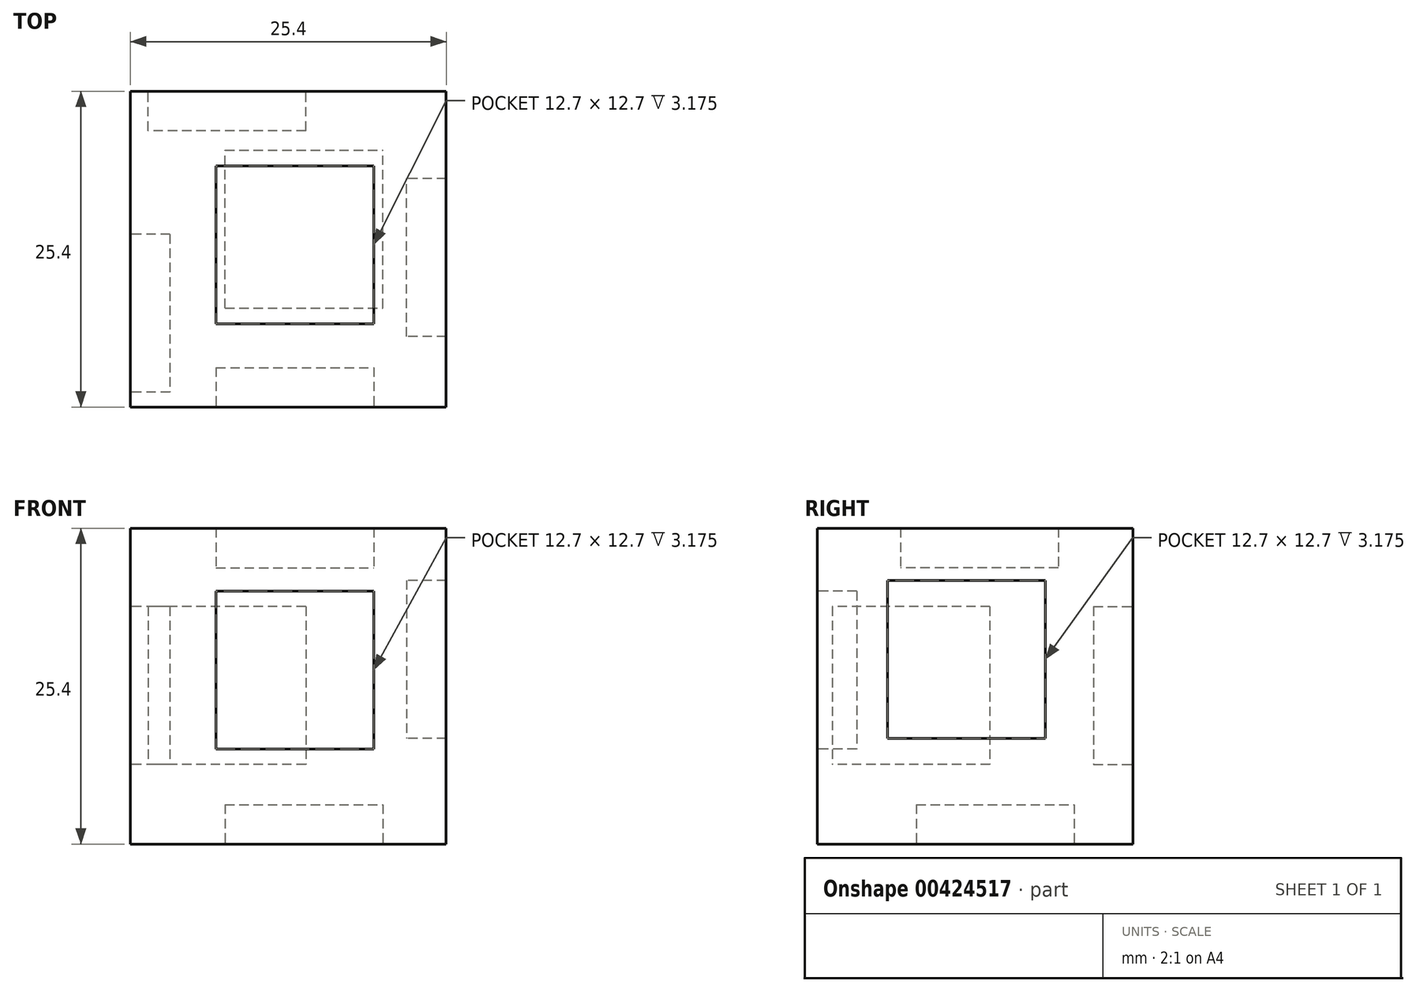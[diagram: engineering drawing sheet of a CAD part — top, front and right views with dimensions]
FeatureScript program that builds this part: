
annotation { "Feature Type Name" : "Feature", "Feature Type Description" : "" }
export const myFeature = defineFeature(function(context is Context, id is Id, definition is map)
    precondition{}
    {
        {
            var Q0;
            Q0=qCreatedBy(makeId("Front.planeOp"),FACE);
            var sketch = newSketch(context, id + "F0", { "sketchPlane" : qUnion([Q0])});
            skLineSegment(sketch, "E0.bottom", {"start": v(-14.1, -6.4) * mm, "end": v(11.3, -6.4) * mm});
            skLineSegment(sketch, "E0.top", {"start": v(-14.1, 19) * mm, "end": v(11.3, 19) * mm});
            skLineSegment(sketch, "E0.left", {"start": v(-14.1, -6.4) * mm, "end": v(-14.1, 19) * mm});
            skLineSegment(sketch, "E0.right", {"start": v(11.3, -6.4) * mm, "end": v(11.3, 19) * mm});
            skSolve(sketch);
        }
        {
            var Q0;
            Q0=makeQuery(id+"F0.imprint","IMPRINT",FACE,{"disambiguationData":[TD([[makeQuery(id+"F0.imprint","IMPRINT",EDGE,{"derivedFrom":sQuery(id+"F0.wireOp",EDGE,"E0.bottom")}),1.0]])]});
            extrude(context, id + "F1", {"entities" : qUnion([Q0]), "depth" : 25.4 * mm});
        }
        {
            var Q0;
            Q0=makeQuery(id+"F1.opExtrude","CAP_FACE",FACE,{"disambiguationData":[OSD([sQuery(id+"F0.wireOp",EDGE,"E0.bottom"),sQuery(id+"F0.wireOp",EDGE,"E0.top"),sQuery(id+"F0.wireOp",EDGE,"E0.left"),sQuery(id+"F0.wireOp",EDGE,"E0.right")])],"isStart":false});
            var sketch = newSketch(context, id + "F2", { "sketchPlane" : qUnion([Q0])});
            skLineSegment(sketch, "E1.bottom", {"start": v(-7.21, 13.93) * mm, "end": v(5.49, 13.93) * mm});
            skLineSegment(sketch, "E1.top", {"start": v(-7.21, 1.23) * mm, "end": v(5.49, 1.23) * mm});
            skLineSegment(sketch, "E1.left", {"start": v(-7.21, 13.93) * mm, "end": v(-7.21, 1.23) * mm});
            skLineSegment(sketch, "E1.right", {"start": v(5.49, 13.93) * mm, "end": v(5.49, 1.23) * mm});
            skSolve(sketch);
        }
        {
            var Q0;
            Q0=makeQuery(id+"F2.imprint","IMPRINT",FACE,{"disambiguationData":[TD([[makeQuery(id+"F2.imprint","IMPRINT",EDGE,{"derivedFrom":sQuery(id+"F2.wireOp",EDGE,"E1.bottom")}),-1.0]])]});
            extrude(context, id + "F3", {"entities" : qUnion([Q0]), "operationType" : NewBodyOperationType.REMOVE, "oppositeDirection" : true, "depth" : 3.17 * mm});
        }
        {
            var Q0;
            Q0=makeQuery(id+"F1.opExtrude","SWEPT_FACE",FACE,{"disambiguationData":[OSD([sQuery(id+"F0.wireOp",EDGE,"E0.bottom")])]});
            var sketch = newSketch(context, id + "F4", { "sketchPlane" : qUnion([Q0])});
            skLineSegment(sketch, "E2.bottom", {"start": v(-6.5, 17.43) * mm, "end": v(6.2, 17.43) * mm});
            skLineSegment(sketch, "E2.top", {"start": v(-6.5, 4.73) * mm, "end": v(6.2, 4.73) * mm});
            skLineSegment(sketch, "E2.left", {"start": v(-6.5, 17.43) * mm, "end": v(-6.5, 4.73) * mm});
            skLineSegment(sketch, "E2.right", {"start": v(6.2, 17.43) * mm, "end": v(6.2, 4.73) * mm});
            skSolve(sketch);
        }
        {
            var Q0;
            Q0=makeQuery(id+"F4.imprint","IMPRINT",FACE,{"disambiguationData":[TD([[makeQuery(id+"F4.imprint","IMPRINT",EDGE,{"derivedFrom":sQuery(id+"F4.wireOp",EDGE,"E2.bottom")}),-1.0]])]});
            extrude(context, id + "F5", {"entities" : qUnion([Q0]), "operationType" : NewBodyOperationType.REMOVE, "oppositeDirection" : true, "depth" : 3.17 * mm});
        }
        {
            var Q0;
            Q0=makeQuery(id+"F1.opExtrude","SWEPT_FACE",FACE,{"disambiguationData":[OSD([sQuery(id+"F0.wireOp",EDGE,"E0.right")])]});
            var sketch = newSketch(context, id + "F6", { "sketchPlane" : qUnion([Q0])});
            skLineSegment(sketch, "E3.bottom", {"start": v(-19.73, 14.8) * mm, "end": v(-7.03, 14.8) * mm});
            skLineSegment(sketch, "E3.top", {"start": v(-19.73, 2.1) * mm, "end": v(-7.03, 2.1) * mm});
            skLineSegment(sketch, "E3.left", {"start": v(-19.73, 14.8) * mm, "end": v(-19.73, 2.1) * mm});
            skLineSegment(sketch, "E3.right", {"start": v(-7.03, 14.8) * mm, "end": v(-7.03, 2.1) * mm});
            skSolve(sketch);
        }
        {
            var Q0;
            Q0=makeQuery(id+"F6.imprint","IMPRINT",FACE,{"disambiguationData":[TD([[makeQuery(id+"F6.imprint","IMPRINT",EDGE,{"derivedFrom":sQuery(id+"F6.wireOp",EDGE,"E3.bottom")}),-1.0]])]});
            extrude(context, id + "F7", {"entities" : qUnion([Q0]), "operationType" : NewBodyOperationType.REMOVE, "oppositeDirection" : true, "depth" : 3.17 * mm});
        }
        {
            var Q0;
            Q0=makeQuery(id+"F1.opExtrude","CAP_FACE",FACE,{"disambiguationData":[OSD([sQuery(id+"F0.wireOp",EDGE,"E0.bottom"),sQuery(id+"F0.wireOp",EDGE,"E0.top"),sQuery(id+"F0.wireOp",EDGE,"E0.left"),sQuery(id+"F0.wireOp",EDGE,"E0.right")])],"isStart":true});
            var sketch = newSketch(context, id + "F8", { "sketchPlane" : qUnion([Q0])});
            skLineSegment(sketch, "E4.bottom", {"start": v(0, 12.7) * mm, "end": v(12.7, 12.7) * mm});
            skLineSegment(sketch, "E4.top", {"start": v(0, 0) * mm, "end": v(12.7, 0) * mm});
            skLineSegment(sketch, "E4.left", {"start": v(0, 12.7) * mm, "end": v(0, 0) * mm});
            skLineSegment(sketch, "E4.right", {"start": v(12.7, 12.7) * mm, "end": v(12.7, 0) * mm});
            skSolve(sketch);
        }
        {
            var Q0;
            Q0=makeQuery(id+"F8.imprint","IMPRINT",FACE,{"disambiguationData":[TD([[makeQuery(id+"F8.imprint","IMPRINT",EDGE,{"derivedFrom":sQuery(id+"F8.wireOp",EDGE,"E4.bottom")}),-1.0]])]});
            extrude(context, id + "F9", {"entities" : qUnion([Q0]), "operationType" : NewBodyOperationType.REMOVE, "oppositeDirection" : true, "depth" : 3.17 * mm});
        }
        {
            var Q0;
            Q0=makeQuery(id+"F1.opExtrude","SWEPT_FACE",FACE,{"disambiguationData":[OSD([sQuery(id+"F0.wireOp",EDGE,"E0.left")])]});
            var sketch = newSketch(context, id + "F10", { "sketchPlane" : qUnion([Q0])});
            skLineSegment(sketch, "E5.bottom", {"start": v(11.5, 12.7) * mm, "end": v(24.2, 12.7) * mm});
            skLineSegment(sketch, "E5.top", {"start": v(11.5, 0) * mm, "end": v(24.2, 0) * mm});
            skLineSegment(sketch, "E5.left", {"start": v(11.5, 12.7) * mm, "end": v(11.5, 0) * mm});
            skLineSegment(sketch, "E5.right", {"start": v(24.2, 12.7) * mm, "end": v(24.2, 0) * mm});
            skSolve(sketch);
        }
        {
            var Q0;
            Q0=makeQuery(id+"F10.imprint","IMPRINT",FACE,{"disambiguationData":[TD([[makeQuery(id+"F10.imprint","IMPRINT",EDGE,{"derivedFrom":sQuery(id+"F10.wireOp",EDGE,"E5.bottom")}),-1.0]])]});
            extrude(context, id + "F11", {"entities" : qUnion([Q0]), "operationType" : NewBodyOperationType.REMOVE, "oppositeDirection" : true, "depth" : 3.17 * mm});
        }
        {
            var Q0;
            Q0=makeQuery(id+"F1.opExtrude","SWEPT_FACE",FACE,{"disambiguationData":[OSD([sQuery(id+"F0.wireOp",EDGE,"E0.top")])]});
            var sketch = newSketch(context, id + "F12", { "sketchPlane" : qUnion([Q0])});
            skLineSegment(sketch, "E6.bottom", {"start": v(-7.21, -6) * mm, "end": v(5.49, -6) * mm});
            skLineSegment(sketch, "E6.top", {"start": v(-7.21, -18.7) * mm, "end": v(5.49, -18.7) * mm});
            skLineSegment(sketch, "E6.left", {"start": v(-7.21, -6) * mm, "end": v(-7.21, -18.7) * mm});
            skLineSegment(sketch, "E6.right", {"start": v(5.49, -6) * mm, "end": v(5.49, -18.7) * mm});
            skSolve(sketch);
        }
        {
            var Q0;
            Q0=makeQuery(id+"F12.imprint","IMPRINT",FACE,{"disambiguationData":[TD([[makeQuery(id+"F12.imprint","IMPRINT",EDGE,{"derivedFrom":sQuery(id+"F12.wireOp",EDGE,"E6.bottom")}),-1.0]])]});
            extrude(context, id + "F13", {"entities" : qUnion([Q0]), "operationType" : NewBodyOperationType.REMOVE, "oppositeDirection" : true, "depth" : 3.17 * mm});
        }
        {
            var Q0;
            Q0=makeQuery(id+"F13.boolean.opBoolean","COPY",FACE,{"derivedFrom":makeQuery(id+"F13.opExtrude","CAP_FACE",FACE,{"disambiguationData":[OSD([sQuery(id+"F12.wireOp",EDGE,"E6.bottom"),sQuery(id+"F12.wireOp",EDGE,"E6.top"),sQuery(id+"F12.wireOp",EDGE,"E6.left"),sQuery(id+"F12.wireOp",EDGE,"E6.right")])],"isStart":false})});
            var sketch = newSketch(context, id + "F14", { "sketchPlane" : qUnion([Q0])});
            skLineSegment(sketch, "E7.bottom", {"start": v(-7.21, -6) * mm, "end": v(5.49, -6) * mm});
            skLineSegment(sketch, "E7.top", {"start": v(-7.21, -18.7) * mm, "end": v(5.49, -18.7) * mm});
            skLineSegment(sketch, "E7.left", {"start": v(-7.21, -6) * mm, "end": v(-7.21, -18.7) * mm});
            skLineSegment(sketch, "E7.right", {"start": v(5.49, -6) * mm, "end": v(5.49, -18.7) * mm});
            skSolve(sketch);
        }
        {
            var Q0;
            Q0 = qSketchRegion(id + "F14", true);
            extrude(context, id + "F15", {"entities" : qUnion([Q0]), "depth" : 3.17 * mm});
        }
        {
            var Q0;
            Q0=makeQuery(id+"F7.boolean.opBoolean","COPY",FACE,{"derivedFrom":makeQuery(id+"F7.opExtrude","CAP_FACE",FACE,{"disambiguationData":[OSD([sQuery(id+"F6.wireOp",EDGE,"E3.bottom"),sQuery(id+"F6.wireOp",EDGE,"E3.top"),sQuery(id+"F6.wireOp",EDGE,"E3.left"),sQuery(id+"F6.wireOp",EDGE,"E3.right")])],"isStart":false})});
            var sketch = newSketch(context, id + "F16", { "sketchPlane" : qUnion([Q0])});
            skLineSegment(sketch, "E8.bottom", {"start": v(-19.73, 14.8) * mm, "end": v(-7.03, 14.8) * mm});
            skLineSegment(sketch, "E8.top", {"start": v(-19.73, 2.1) * mm, "end": v(-7.03, 2.1) * mm});
            skLineSegment(sketch, "E8.left", {"start": v(-19.73, 14.8) * mm, "end": v(-19.73, 2.1) * mm});
            skLineSegment(sketch, "E8.right", {"start": v(-7.03, 14.8) * mm, "end": v(-7.03, 2.1) * mm});
            skSolve(sketch);
        }
        {
            var Q0;
            Q0 = qSketchRegion(id + "F16", true);
            extrude(context, id + "F17", {"entities" : qUnion([Q0]), "depth" : 3.17 * mm});
        }
        {
            var Q0;
            Q0=makeQuery(id+"F9.boolean.opBoolean","COPY",FACE,{"derivedFrom":makeQuery(id+"F9.opExtrude","CAP_FACE",FACE,{"disambiguationData":[OSD([sQuery(id+"F8.wireOp",EDGE,"E4.bottom"),sQuery(id+"F8.wireOp",EDGE,"E4.top"),sQuery(id+"F8.wireOp",EDGE,"E4.left"),sQuery(id+"F8.wireOp",EDGE,"E4.right")])],"isStart":false})});
            var sketch = newSketch(context, id + "F18", { "sketchPlane" : qUnion([Q0])});
            skLineSegment(sketch, "E9.bottom", {"start": v(0, 12.7) * mm, "end": v(12.7, 12.7) * mm});
            skLineSegment(sketch, "E9.top", {"start": v(0, 0) * mm, "end": v(12.7, 0) * mm});
            skLineSegment(sketch, "E9.left", {"start": v(0, 12.7) * mm, "end": v(0, 0) * mm});
            skLineSegment(sketch, "E9.right", {"start": v(12.7, 12.7) * mm, "end": v(12.7, 0) * mm});
            skSolve(sketch);
        }
        {
            var Q0;
            Q0 = qSketchRegion(id + "F18", true);
            extrude(context, id + "F19", {"entities" : qUnion([Q0]), "depth" : 3.17 * mm});
        }
        {
            var Q0;
            Q0=makeQuery(id+"F11.boolean.opBoolean","COPY",FACE,{"derivedFrom":makeQuery(id+"F11.opExtrude","CAP_FACE",FACE,{"disambiguationData":[OSD([sQuery(id+"F10.wireOp",EDGE,"E5.bottom"),sQuery(id+"F10.wireOp",EDGE,"E5.top"),sQuery(id+"F10.wireOp",EDGE,"E5.left"),sQuery(id+"F10.wireOp",EDGE,"E5.right")])],"isStart":false})});
            var sketch = newSketch(context, id + "F20", { "sketchPlane" : qUnion([Q0])});
            skLineSegment(sketch, "E10.bottom", {"start": v(11.5, 12.7) * mm, "end": v(24.2, 12.7) * mm});
            skLineSegment(sketch, "E10.top", {"start": v(11.5, 0) * mm, "end": v(24.2, 0) * mm});
            skLineSegment(sketch, "E10.left", {"start": v(11.5, 12.7) * mm, "end": v(11.5, 0) * mm});
            skLineSegment(sketch, "E10.right", {"start": v(24.2, 12.7) * mm, "end": v(24.2, 0) * mm});
            skSolve(sketch);
        }
        {
            var Q0;
            Q0 = qSketchRegion(id + "F20", true);
            extrude(context, id + "F21", {"entities" : qUnion([Q0]), "depth" : 3.17 * mm});
        }
        {
            var Q0;
            Q0=makeQuery(id+"F3.boolean.opBoolean","COPY",FACE,{"derivedFrom":makeQuery(id+"F3.opExtrude","CAP_FACE",FACE,{"disambiguationData":[OSD([sQuery(id+"F2.wireOp",EDGE,"E1.bottom"),sQuery(id+"F2.wireOp",EDGE,"E1.top"),sQuery(id+"F2.wireOp",EDGE,"E1.left"),sQuery(id+"F2.wireOp",EDGE,"E1.right")])],"isStart":false})});
            var sketch = newSketch(context, id + "F22", { "sketchPlane" : qUnion([Q0])});
            skLineSegment(sketch, "E11.bottom", {"start": v(-7.21, 13.93) * mm, "end": v(5.49, 13.93) * mm});
            skLineSegment(sketch, "E11.top", {"start": v(-7.21, 1.23) * mm, "end": v(5.49, 1.23) * mm});
            skLineSegment(sketch, "E11.left", {"start": v(-7.21, 13.93) * mm, "end": v(-7.21, 1.23) * mm});
            skLineSegment(sketch, "E11.right", {"start": v(5.49, 13.93) * mm, "end": v(5.49, 1.23) * mm});
            skSolve(sketch);
        }
        {
            var Q0;
            Q0 = qSketchRegion(id + "F22", true);
            extrude(context, id + "F23", {"entities" : qUnion([Q0]), "depth" : 3.17 * mm});
        }
        {
            var Q0;
            Q0=makeQuery(id+"F5.boolean.opBoolean","COPY",FACE,{"derivedFrom":makeQuery(id+"F5.opExtrude","CAP_FACE",FACE,{"disambiguationData":[OSD([sQuery(id+"F4.wireOp",EDGE,"E2.bottom"),sQuery(id+"F4.wireOp",EDGE,"E2.top"),sQuery(id+"F4.wireOp",EDGE,"E2.left"),sQuery(id+"F4.wireOp",EDGE,"E2.right")])],"isStart":false})});
            var sketch = newSketch(context, id + "F24", { "sketchPlane" : qUnion([Q0])});
            skLineSegment(sketch, "E12.bottom", {"start": v(-6.5, 17.43) * mm, "end": v(6.2, 17.43) * mm});
            skLineSegment(sketch, "E12.top", {"start": v(-6.5, 4.73) * mm, "end": v(6.2, 4.73) * mm});
            skLineSegment(sketch, "E12.left", {"start": v(-6.5, 17.43) * mm, "end": v(-6.5, 4.73) * mm});
            skLineSegment(sketch, "E12.right", {"start": v(6.2, 17.43) * mm, "end": v(6.2, 4.73) * mm});
            skSolve(sketch);
        }
        {
            var Q0;
            Q0 = qSketchRegion(id + "F24", true);
            extrude(context, id + "F25", {"entities" : qUnion([Q0]), "depth" : 3.17 * mm});
        }
    });
